# Revit family: CLUSTER
name_source: partatom
category: Arredi
units: mm (PartAtom-declared; Revit-internal decimal feet)

## family parameters
Basato su piano di lavoro = Sì
Condiviso = No
Punto di calcolo locali = No
Sempre verticale = Sì
Taglio con vuoti quando caricato = No

## types (26) — shared parameters
Prospetto di default = 1219 mm

## per-type parameters (varying)
| type | 1A | 1B | 2A | 2B | 3A | 3B | Altezza seduta | G_CL1 | G_CL10 | G_CL2 | G_CL3 | G_CL4 | G_CL7_8 | Imbottiture | Struttura |
| CL1_D | Sì | No | Sì | No | No | No | 412 mm | Sì | No | No | No | No | No | 3518_Luxy_Imbottiture | 3518_Luxy_Struttura |
| CL1_E | Sì | No | No | Sì | No | No | 412 mm | Sì | No | No | No | No | No | 3518_Luxy_Imbottiture | 3518_Luxy_Struttura |
| CL1_F | Sì | No | Sì | No | Sì | No | 412 mm | Sì | No | No | No | No | No | 3518_Luxy_Imbottiture | 3518_Luxy_Struttura |
| CL1_G | Sì | No | No | Sì | Sì | No | 412 mm | Sì | No | No | No | No | No | 3518_Luxy_Imbottiture | 3518_Luxy_Struttura |
| CL2_D | Sì | No | Sì | No | No | No | 404 mm | No | No | Sì | No | No | No | <Per categoria> | <Per categoria> |
| CL2_E | Sì | No | No | Sì | No | No | 404 mm | No | No | Sì | No | No | No | <Per categoria> | <Per categoria> |
| CL2_F | Sì | No | Sì | No | Sì | No | 404 mm | No | No | Sì | No | No | No | <Per categoria> | <Per categoria> |
| CL2_G | Sì | No | No | Sì | Sì | No | 404 mm | No | No | Sì | No | No | No | <Per categoria> | <Per categoria> |
| CL3_D | Sì | No | Sì | No | No | No | 392 mm | No | No | No | Sì | No | No | <Per categoria> | <Per categoria> |
| CL3_E | Sì | No | No | Sì | No | No | 392 mm | No | No | No | Sì | No | No | <Per categoria> | <Per categoria> |
| CL3_F | Sì | No | Sì | No | Sì | No | 392 mm | No | No | No | Sì | No | No | <Per categoria> | <Per categoria> |
| CL3_G | Sì | No | No | Sì | Sì | No | 392 mm | No | No | No | Sì | No | No | <Per categoria> | <Per categoria> |
| CL4_D | Sì | No | Sì | No | No | No | 386 mm | No | No | No | No | Sì | No | <Per categoria> | <Per categoria> |
| CL4_E | Sì | No | No | Sì | No | No | 386 mm | No | No | No | No | Sì | No | <Per categoria> | <Per categoria> |
| CL4_F | Sì | No | Sì | No | Sì | No | 386 mm | No | No | No | No | Sì | No | <Per categoria> | <Per categoria> |
| CL4_G | Sì | No | No | Sì | Sì | No | 386 mm | No | No | No | No | Sì | No | <Per categoria> | <Per categoria> |
| CL4_H | No | Sì | No | Sì | No | Sì | 386 mm | No | No | No | No | Sì | No | <Per categoria> | <Per categoria> |
| CL10_D | Sì | No | Sì | No | No | No | 762 mm | No | Sì | No | No | No | No | <Per categoria> | <Per categoria> |
| CL10_E | Sì | No | No | Sì | No | No | 762 mm | No | Sì | No | No | No | No | <Per categoria> | <Per categoria> |
| CL10_C | No | Sì | No | No | No | No | 762 mm | No | Sì | No | No | No | No | <Per categoria> | <Per categoria> |
| CL10_B | Sì | No | No | No | No | No | 762 mm | No | Sì | No | No | No | No | <Per categoria> | <Per categoria> |
| CL10_A | No | No | No | No | No | No | 762 mm | No | Sì | No | No | No | No | 3518_Luxy_Imbottiture | 3518_Luxy_Struttura |
| CL7_8_D | Sì | No | Sì | No | No | No | 450 mm | No | No | No | No | No | Sì | <Per categoria> | <Per categoria> |
| CL7_8_E | Sì | No | No | Sì | No | No | 450 mm | No | No | No | No | No | Sì | <Per categoria> | <Per categoria> |
| CL7_8_F | Sì | No | Sì | No | Sì | No | 450 mm | No | No | No | No | No | Sì | 3518_Luxy_Imbottiture | 3518_Luxy_Struttura |
| CL7_8_G | Sì | No | No | Sì | Sì | No | 450 mm | No | No | No | No | No | Sì | <Per categoria> | <Per categoria> |

## geometry (parser evidence)
native form markers: Sweep x6
no freeform markers — native parametric forms only
